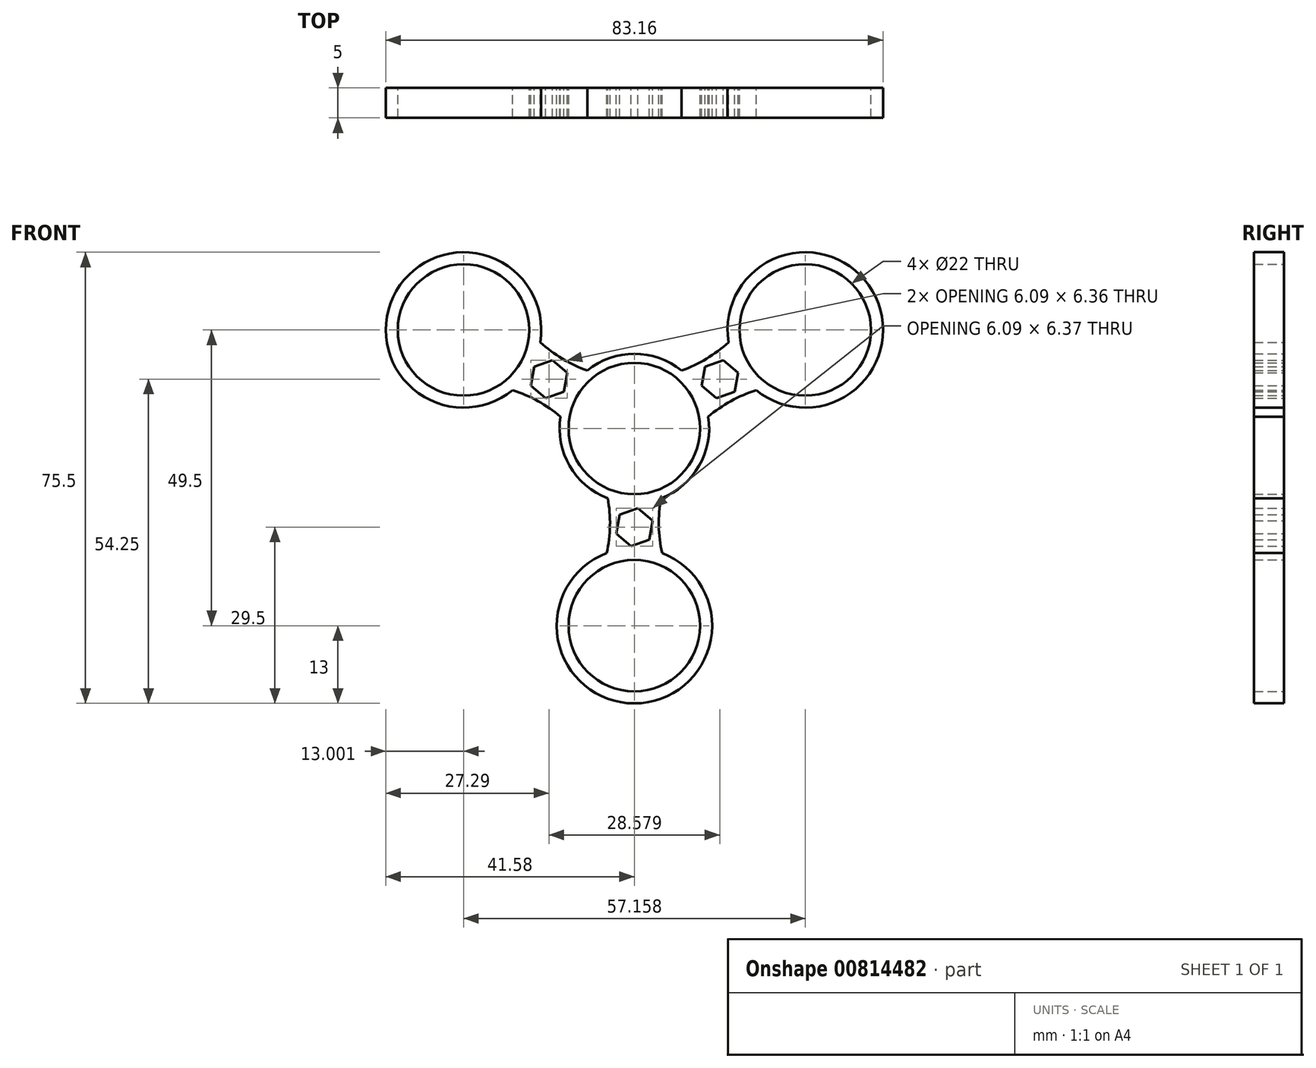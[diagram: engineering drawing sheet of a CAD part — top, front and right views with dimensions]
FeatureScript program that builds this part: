
annotation { "Feature Type Name" : "Feature", "Feature Type Description" : "" }
export const myFeature = defineFeature(function(context is Context, id is Id, definition is map)
    precondition{}
    {
        {
            var Q0;
            Q0=qCreatedBy(makeId("Front.planeOp"),FACE);
            var sketch = newSketch(context, id + "F0", { "sketchPlane" : qUnion([Q0])});
            skCircle(sketch, "E0", {"center": v(0, 0) * mm, "radius": 11 * mm});
            skLineSegment(sketch, "E1", {"start": v(11.71, 6.76) * mm, "end": v(11.86, 6.85) * mm});
            skArc(sketch, "E2", {"start": v(20.37, 6.42) * mm, "mid": v(39.84, 23) * mm, "end": v(15.74, 14.43) * mm});
            skCircle(sketch, "E3", {"center": v(28.58, 16.5) * mm, "radius": 11 * mm});
            skArc(sketch, "E4.trimOffspring", {"start": v(7.89, 9.7) * mm, "mid": v(12.05, 11.67) * mm, "end": v(15.74, 14.43) * mm});
            skArc(sketch, "E5.MirrorCS", {"start": v(12.34, 1.98) * mm, "mid": v(16.14, 4.6) * mm, "end": v(20.37, 6.42) * mm});
            skArc(sketch, "E6.2.1", {"start": v(-12.34, 1.98) * mm, "mid": v(-10.83, -6.25) * mm, "end": v(-4.45, -11.68) * mm});
            skArc(sketch, "E7.1.0", {"start": v(-12.34, 1.98) * mm, "mid": v(-16.14, 4.6) * mm, "end": v(-20.37, 6.42) * mm});
            skArc(sketch, "E7.1.1", {"start": v(-15.74, 14.43) * mm, "mid": v(-39.84, 23) * mm, "end": v(-20.37, 6.42) * mm});
            skArc(sketch, "E7.1.3", {"start": v(-7.89, 9.7) * mm, "mid": v(-12.05, 11.67) * mm, "end": v(-15.74, 14.43) * mm});
            skArc(sketch, "E7.2.0", {"start": v(4.45, -11.68) * mm, "mid": v(4.08, -16.27) * mm, "end": v(4.63, -20.85) * mm});
            skArc(sketch, "E7.2.1", {"start": v(-4.63, -20.85) * mm, "mid": v(0, -46) * mm, "end": v(4.63, -20.85) * mm});
            skLineSegment(sketch, "E7.2.2", {"start": v(0, -13.52) * mm, "end": v(0, -13.7) * mm});
            skArc(sketch, "E7.2.3", {"start": v(-4.45, -11.68) * mm, "mid": v(-4.08, -16.27) * mm, "end": v(-4.63, -20.85) * mm});
            skCircle(sketch, "E8.1.0", {"center": v(-28.58, 16.5) * mm, "radius": 11 * mm});
            skCircle(sketch, "E8.2.0", {"center": v(0, -33) * mm, "radius": 11 * mm});
            skArc(sketch, "E9.trimOffspring", {"start": v(7.89, 9.7) * mm, "mid": v(0, 12.5) * mm, "end": v(-7.89, 9.7) * mm});
            skCircle(sketch, "E10.cCircle", {"center": v(14.29, 8.25) * mm, "radius": 2.8 * mm, "construction": true});
            skLineSegment(sketch, "E10.0", {"start": v(16.76, 6.16) * mm, "end": v(13.71, 5.07) * mm});
            skLineSegment(sketch, "E10.1", {"start": v(13.71, 5.07) * mm, "end": v(11.24, 7.16) * mm});
            skLineSegment(sketch, "E10.2", {"start": v(11.24, 7.16) * mm, "end": v(11.82, 10.34) * mm});
            skLineSegment(sketch, "E10.3", {"start": v(11.82, 10.34) * mm, "end": v(14.87, 11.43) * mm});
            skLineSegment(sketch, "E10.4", {"start": v(14.87, 11.43) * mm, "end": v(17.33, 9.34) * mm});
            skLineSegment(sketch, "E10.5", {"start": v(17.33, 9.34) * mm, "end": v(16.76, 6.16) * mm});
            skPoint(sketch, "E10.0.midPoint", {"position": v(15.23, 5.61) * mm});
            skLineSegment(sketch, "E11.1.0", {"start": v(-14.87, 5.07) * mm, "end": v(-17.33, 7.16) * mm});
            skLineSegment(sketch, "E11.1.1", {"start": v(-17.33, 7.16) * mm, "end": v(-16.76, 10.34) * mm});
            skLineSegment(sketch, "E11.1.2", {"start": v(-16.76, 10.34) * mm, "end": v(-13.71, 11.43) * mm});
            skLineSegment(sketch, "E11.1.3", {"start": v(-13.71, 11.43) * mm, "end": v(-11.24, 9.34) * mm});
            skLineSegment(sketch, "E11.1.4", {"start": v(-11.82, 6.16) * mm, "end": v(-14.87, 5.07) * mm});
            skCircle(sketch, "E11.1.5", {"center": v(-14.29, 8.25) * mm, "radius": 2.8 * mm, "construction": true});
            skLineSegment(sketch, "E11.1.6", {"start": v(-11.24, 9.34) * mm, "end": v(-11.82, 6.16) * mm});
            skLineSegment(sketch, "E11.2.0", {"start": v(3.05, -15.4) * mm, "end": v(2.47, -18.6) * mm});
            skLineSegment(sketch, "E11.2.1", {"start": v(2.47, -18.6) * mm, "end": v(-0.58, -19.68) * mm});
            skLineSegment(sketch, "E11.2.2", {"start": v(-0.58, -19.68) * mm, "end": v(-3.05, -17.6) * mm});
            skLineSegment(sketch, "E11.2.3", {"start": v(-3.05, -17.6) * mm, "end": v(-2.47, -14.4) * mm});
            skLineSegment(sketch, "E11.2.4", {"start": v(0.58, -13.32) * mm, "end": v(3.05, -15.4) * mm});
            skCircle(sketch, "E11.2.5", {"center": v(0, -16.5) * mm, "radius": 2.8 * mm, "construction": true});
            skLineSegment(sketch, "E11.2.6", {"start": v(-2.47, -14.4) * mm, "end": v(0.58, -13.32) * mm});
            skLineSegment(sketch, "E12.trimOffspring", {"start": v(16.72, 9.65) * mm, "end": v(16.87, 9.74) * mm});
            skArc(sketch, "E13.trimOffspring", {"start": v(4.45, -11.68) * mm, "mid": v(10.83, -6.25) * mm, "end": v(12.34, 1.98) * mm});
            skLineSegment(sketch, "E14.trimOffspring", {"start": v(0, -19.3) * mm, "end": v(0, -19.48) * mm});
            skSolve(sketch);
        }
        {
            var Q0;
            Q0 = qSketchRegion(id + "F0", true);
            extrude(context, id + "F1", {"entities" : qUnion([Q0]), "flatOperationType" : FlatOperationType.REMOVE, "depth" : 5 * mm, "offsetDistance" : 25 * mm, "domain" : OperationDomain.MODEL});
        }
    });
